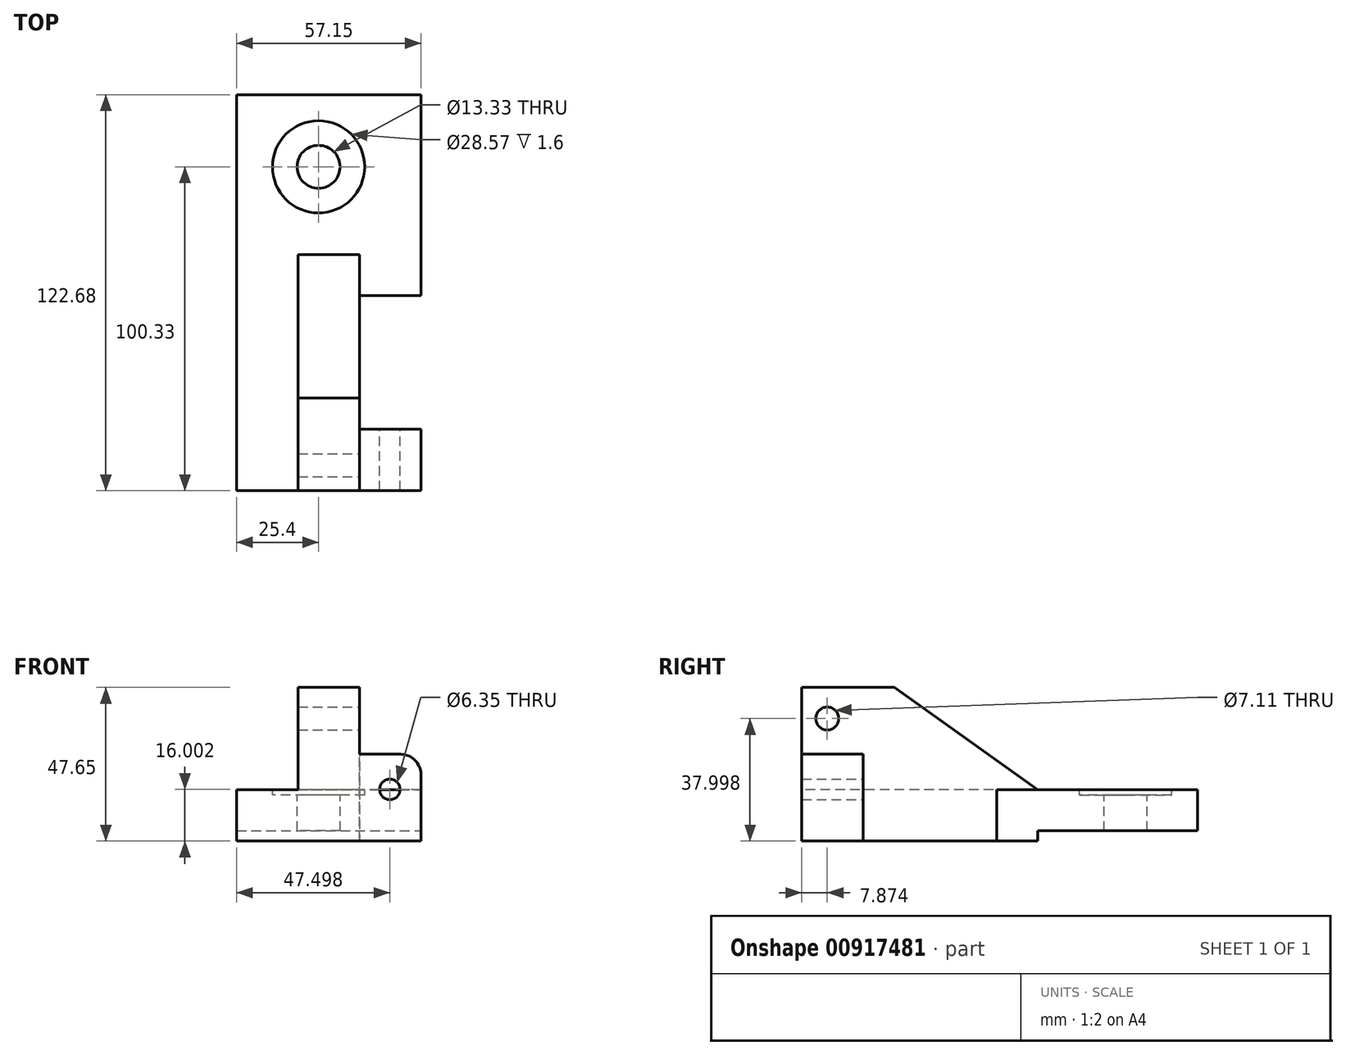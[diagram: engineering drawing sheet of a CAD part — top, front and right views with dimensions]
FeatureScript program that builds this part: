
annotation { "Feature Type Name" : "Feature", "Feature Type Description" : "" }
export const myFeature = defineFeature(function(context is Context, id is Id, definition is map)
    precondition{}
    {
        {
            var Q0;
            Q0=qCreatedBy(makeId("Right.planeOp"),FACE);
            var sketch = newSketch(context, id + "F0", { "sketchPlane" : qUnion([Q0])});
            skLineSegment(sketch, "E0", {"start": v(0, 0) * mm, "end": v(73.15, 0) * mm});
            skLineSegment(sketch, "E1", {"start": v(0, 0) * mm, "end": v(0, 47.65) * mm});
            skLineSegment(sketch, "E2", {"start": v(0, 47.65) * mm, "end": v(28.7, 47.65) * mm});
            skLineSegment(sketch, "E3", {"start": v(73.15, 0) * mm, "end": v(73.15, 15.88) * mm});
            skLineSegment(sketch, "E4", {"start": v(28.7, 47.65) * mm, "end": v(73.15, 15.87) * mm});
            skLineSegment(sketch, "E5", {"start": v(73.15, 15.88) * mm, "end": v(0, 15.88) * mm});
            skSolve(sketch);
        }
        {
            var Q0;
            {var subQ0=sQuery(id+"F0.wireOp",EDGE,"E2");Q0=makeQuery(id+"F0.imprint","IMPRINT",FACE,{"disambiguationData":[TD([[makeQuery(id+"F0.imprint","IMPRINT",EDGE,{"derivedFrom":subQ0}),-1.0]])]});}
            var Q1;
            {var subQ0=sQuery(id+"F0.wireOp",EDGE,"E0");Q1=makeQuery(id+"F0.imprint","IMPRINT",FACE,{"disambiguationData":[TD([[makeQuery(id+"F0.imprint","IMPRINT",EDGE,{"derivedFrom":subQ0}),1.0]])]});}
            extrude(context, id + "F1", {"entities" : qUnion([Q0, Q1]), "depth" : 19.05 * mm, "offsetDistance" : 25.4 * mm});
        }
        {
            var Q0;
            Q0=makeQuery(id+"F1.opExtrude","CAP_FACE",FACE,{"disambiguationData":[OSD([sQuery(id+"F0.wireOp",EDGE,"E0"),sQuery(id+"F0.wireOp",EDGE,"E1"),sQuery(id+"F0.wireOp",EDGE,"E2"),sQuery(id+"F0.wireOp",EDGE,"mmEop4HQ-drAs-Js47-yDfj-Hc2bwHA6L0MF")])],"isStart":false});
            var sketch = newSketch(context, id + "F2", { "sketchPlane" : qUnion([Q0])});
            skPoint(sketch, "E6", {"position": v(7.87, 38) * mm});
            skSolve(sketch);
        }
        {
            var Q0;
            Q0=sQuery(id+"F2.wireOp",VERTEX,"E6");
            var Q1;
            Q1=makeQuery(id+"F1.opExtrude","SWEPT_BODY",BODY,{"disambiguationData":[OSD([sQuery(id+"F0.wireOp",EDGE,"E0"),sQuery(id+"F0.wireOp",EDGE,"E1"),sQuery(id+"F0.wireOp",EDGE,"E2"),sQuery(id+"F0.wireOp",EDGE,"mmEop4HQ-drAs-Js47-yDfj-Hc2bwHA6L0MF")])]});
            hole(context, id + "F3", {"style" : HoleStyle.SIMPLE, "endStyle" : HoleEndStyle.THROUGH, "holeDiameter" : 7.11 * mm, "majorDiameter" : 6.35 * mm, "isTappedThrough" : true, "tappedDepth" : 12.7 * mm, "tapClearance" : 3, "locations" : qUnion([Q0]), "scope" : qUnion([Q1])});
        }
        {
            var Q0;
            Q0=makeQuery(id+"F1.opExtrude","CAP_FACE",FACE,{"disambiguationData":[OSD([sQuery(id+"F0.wireOp",EDGE,"E0"),sQuery(id+"F0.wireOp",EDGE,"E1"),sQuery(id+"F0.wireOp",EDGE,"E2"),sQuery(id+"F0.wireOp",EDGE,"mmEop4HQ-drAs-Js47-yDfj-Hc2bwHA6L0MF")])],"isStart":false});
            var sketch = newSketch(context, id + "F4", { "sketchPlane" : qUnion([Q0])});
            skLineSegment(sketch, "E7", {"start": v(0, 0) * mm, "end": v(19.05, 0) * mm});
            skLineSegment(sketch, "E8", {"start": v(19.05, 0) * mm, "end": v(19.05, 26.92) * mm});
            skLineSegment(sketch, "E9", {"start": v(19.05, 26.92) * mm, "end": v(0, 26.92) * mm});
            skSolve(sketch);
        }
        {
            var Q0;
            {var subQ0=sQuery(id+"F4.wireOp",EDGE,"E7");Q0=makeQuery(id+"F4.imprint","IMPRINT",FACE,{"disambiguationData":[TD([[makeQuery(id+"F4.imprint","IMPRINT",EDGE,{"derivedFrom":subQ0}),1.0]])]});}
            extrude(context, id + "F5", {"entities" : qUnion([Q0]), "operationType" : NewBodyOperationType.ADD, "depth" : 19.05 * mm, "offsetDistance" : 25.4 * mm});
        }
        {
            var Q0;
            Q0=makeQuery(id+"F5.opExtrude","SWEPT_FACE",FACE,{"disambiguationData":[OSD([sQuery(id+"F4.wireOp",EDGE,"E8")])]});
            var sketch = newSketch(context, id + "F6", { "sketchPlane" : qUnion([Q0])});
            skPoint(sketch, "E10", {"position": v(-28.45, 16) * mm});
            skCircle(sketch, "E11", {"center": v(-31.75, 20.57) * mm, "radius": 6.35 * mm});
            skSolve(sketch);
        }
        {
            var Q0;
            Q0=sQuery(id+"F6.wireOp",VERTEX,"E10");
            var Q1;
            Q1=makeQuery(id+"F1.opExtrude","SWEPT_BODY",BODY,{"disambiguationData":[OSD([sQuery(id+"F0.wireOp",EDGE,"E0"),sQuery(id+"F0.wireOp",EDGE,"E1"),sQuery(id+"F0.wireOp",EDGE,"E2"),sQuery(id+"F0.wireOp",EDGE,"mmEop4HQ-drAs-Js47-yDfj-Hc2bwHA6L0MF")])]});
            hole(context, id + "F7", {"style" : HoleStyle.SIMPLE, "endStyle" : HoleEndStyle.THROUGH, "holeDiameter" : 6.35 * mm, "majorDiameter" : 6.35 * mm, "isTappedThrough" : true, "tappedDepth" : 12.7 * mm, "tapClearance" : 3, "locations" : qUnion([Q0]), "scope" : qUnion([Q1])});
        }
        {
            var Q0;
            {var subQ0=sQuery(id+"F0.wireOp",EDGE,"E0");Q0=makeQuery(id+"F0.imprint","IMPRINT",FACE,{"disambiguationData":[TD([[makeQuery(id+"F0.imprint","IMPRINT",EDGE,{"derivedFrom":subQ0}),1.0]])]});}
            extrude(context, id + "F8", {"entities" : qUnion([Q0]), "oppositeDirection" : true, "depth" : 19.05 * mm, "offsetDistance" : 25.4 * mm});
        }
        {
            var Q0;
            Q0=makeQuery(id+"F8.opExtrude","SWEPT_FACE",FACE,{"disambiguationData":[OSD([sQuery(id+"F0.wireOp",EDGE,"E3")])]});
            extrude(context, id + "F9", {"entities" : qUnion([Q0]), "depth" : 49.53 * mm, "offsetDistance" : 25.4 * mm});
        }
        {
            var Q0;
            {var subQ0=sQuery(id+"F0.wireOp",EDGE,"E3");Q0=makeQuery(id+"F9.opExtrude","SWEPT_FACE",FACE,{"disambiguationData":[OSD([subQ0]),TDD([makeQuery(id+"F8.opExtrude","CAP_EDGE",EDGE,{"disambiguationData":[OSD([subQ0])],"isStart":true})])]});}
            extrude(context, id + "F10", {"entities" : qUnion([Q0]), "depth" : 38.1 * mm, "offsetDistance" : 25.4 * mm});
        }
        {
            var Q0;
            {var subQ0=sQuery(id+"F0.wireOp",EDGE,"E3");Q0=makeQuery(id+"F10.opExtrude","SWEPT_FACE",FACE,{"disambiguationData":[OSD([subQ0]),TDD([makeQuery(id+"F9.opExtrude","CAP_EDGE",EDGE,{"disambiguationData":[OSD([subQ0]),TDD([makeQuery(id+"F8.opExtrude","CAP_EDGE",EDGE,{"disambiguationData":[OSD([subQ0])],"isStart":true})])],"isStart":true})])]});}
            extrude(context, id + "F11", {"entities" : qUnion([Q0]), "depth" : 12.7 * mm, "offsetDistance" : 25.4 * mm});
        }
        {
            var Q0;
            Q0=makeQuery(id+"F1.opExtrude","SWEPT_BODY",BODY,{"disambiguationData":[OSD([sQuery(id+"F0.wireOp",EDGE,"E0"),sQuery(id+"F0.wireOp",EDGE,"E1"),sQuery(id+"F0.wireOp",EDGE,"E2"),sQuery(id+"F0.wireOp",EDGE,"E3"),sQuery(id+"F0.wireOp",EDGE,"E4")])]});
            var Q1;
            Q1=makeQuery(id+"F8.opExtrude","SWEPT_BODY",BODY,{"disambiguationData":[OSD([sQuery(id+"F0.wireOp",EDGE,"E0"),sQuery(id+"F0.wireOp",EDGE,"E1"),sQuery(id+"F0.wireOp",EDGE,"E3"),sQuery(id+"F0.wireOp",EDGE,"E5")])]});
            var Q2;
            Q2=makeQuery(id+"F9.opExtrude","SWEPT_BODY",BODY,{"disambiguationData":[OSD([sQuery(id+"F0.wireOp",EDGE,"E3")])]});
            var Q3;
            Q3=makeQuery(id+"F10.opExtrude","SWEPT_BODY",BODY,{"disambiguationData":[OSD([sQuery(id+"F0.wireOp",EDGE,"E3")])]});
            var Q4;
            Q4=makeQuery(id+"F11.opExtrude","SWEPT_BODY",BODY,{"disambiguationData":[OSD([sQuery(id+"F0.wireOp",EDGE,"E3")])]});
            booleanBodies(context, id + "F12", {"operationType" : BooleanOperationType.UNION, "tools" : qUnion([Q0, Q1, Q2, Q3, Q4])});
        }
        {
            var Q0;
            Q0=qCreatedBy(makeId("Top.planeOp"),FACE);
            var sketch = newSketch(context, id + "F13", { "sketchPlane" : qUnion([Q0])});
            skLineSegment(sketch, "E12", {"start": v(-19.05, 73.15) * mm, "end": v(38.1, 73.15) * mm});
            skLineSegment(sketch, "E13", {"start": v(-19.05, 73.15) * mm, "end": v(-19.05, 122.68) * mm});
            skLineSegment(sketch, "E14", {"start": v(-19.05, 122.68) * mm, "end": v(38.1, 122.68) * mm});
            skLineSegment(sketch, "E15", {"start": v(38.1, 73.15) * mm, "end": v(38.1, 122.68) * mm});
            skSolve(sketch);
        }
        {
            var Q0;
            Q0=makeQuery(id+"F13.imprint","IMPRINT",FACE,{"disambiguationData":[TD([[makeQuery(id+"F13.imprint","IMPRINT",EDGE,{"derivedFrom":sQuery(id+"F13.wireOp",EDGE,"E12")}),1.0]])]});
            extrude(context, id + "F14", {"entities" : qUnion([Q0]), "operationType" : NewBodyOperationType.REMOVE, "depth" : 3.17 * mm, "offsetDistance" : 25.4 * mm});
        }
        {
            var Q0;
            {var subQ0=sQuery(id+"F0.wireOp",EDGE,"E5");var subQ1=sQuery(id+"F0.wireOp",EDGE,"E4");var subQ2=sQuery(id+"F0.wireOp",EDGE,"E3");Q0=makeQuery(id+"F12.opBoolean","MERGE",FACE,{"derivedFrom":[makeQuery(id+"F8.opExtrude","SWEPT_FACE",FACE,{"disambiguationData":[OSD([subQ0])]}),makeQuery(id+"F9.opExtrude","SWEPT_FACE",FACE,{"disambiguationData":[OSD([subQ2,subQ1,subQ0])]}),makeQuery(id+"F10.opExtrude","SWEPT_FACE",FACE,{"disambiguationData":[OSD([subQ2,subQ1,subQ0])]}),makeQuery(id+"F11.opExtrude","SWEPT_FACE",FACE,{"disambiguationData":[OSD([subQ2,subQ1,subQ0])]})]});}
            var sketch = newSketch(context, id + "F15", { "sketchPlane" : qUnion([Q0])});
            skPoint(sketch, "E16", {"position": v(6.35, 100.33) * mm});
            skPoint(sketch, "E16.positionSnap0", {"position": v(9.52, 122.68) * mm});
            skSolve(sketch);
        }
        {
            var Q0;
            Q0=sQuery(id+"F15.wireOp",VERTEX,"E16");
            var Q1;
            Q1=makeQuery(id+"F1.opExtrude","SWEPT_BODY",BODY,{"disambiguationData":[OSD([sQuery(id+"F0.wireOp",EDGE,"E0"),sQuery(id+"F0.wireOp",EDGE,"E1"),sQuery(id+"F0.wireOp",EDGE,"E2"),sQuery(id+"F0.wireOp",EDGE,"E3"),sQuery(id+"F0.wireOp",EDGE,"E4")])]});
            hole(context, id + "F16", {"style" : HoleStyle.C_BORE, "endStyle" : HoleEndStyle.THROUGH, "holeDiameter" : 13.33 * mm, "cBoreDiameter" : 28.57 * mm, "cBoreDepth" : 1.6 * mm, "majorDiameter" : 6.35 * mm, "isTappedThrough" : true, "tappedDepth" : 12.7 * mm, "tapClearance" : 3, "locations" : qUnion([Q0]), "scope" : qUnion([Q1])});
        }
        {
            var Q0;
            {var subQ0=sQuery(id+"F6.wireOp",EDGE,"E11");var subQ1=sQuery(id+"F4.wireOp",EDGE,"E8");var subQ4=makeQuery(id+"F5.opExtrude","CAP_EDGE",EDGE,{"disambiguationData":[OSD([subQ1])],"isStart":false});var subQ5=makeQuery(id+"F6.imprint","INTERSECT",VERTEX,{"derivedFrom":[subQ4,subQ0]});Q0=makeQuery(id+"F6.imprint","IMPRINT",FACE,{"disambiguationData":[TD([[makeQuery(id+"F6.imprint","IMPRINT",EDGE,{"disambiguationData":[TD([[subQ5,1.0]])],"derivedFrom":subQ0}),-1.0]])]});}
            extrude(context, id + "F17", {"entities" : qUnion([Q0]), "operationType" : NewBodyOperationType.REMOVE, "oppositeDirection" : true, "depth" : 25.4 * mm, "offsetDistance" : 25.4 * mm});
        }
    });
